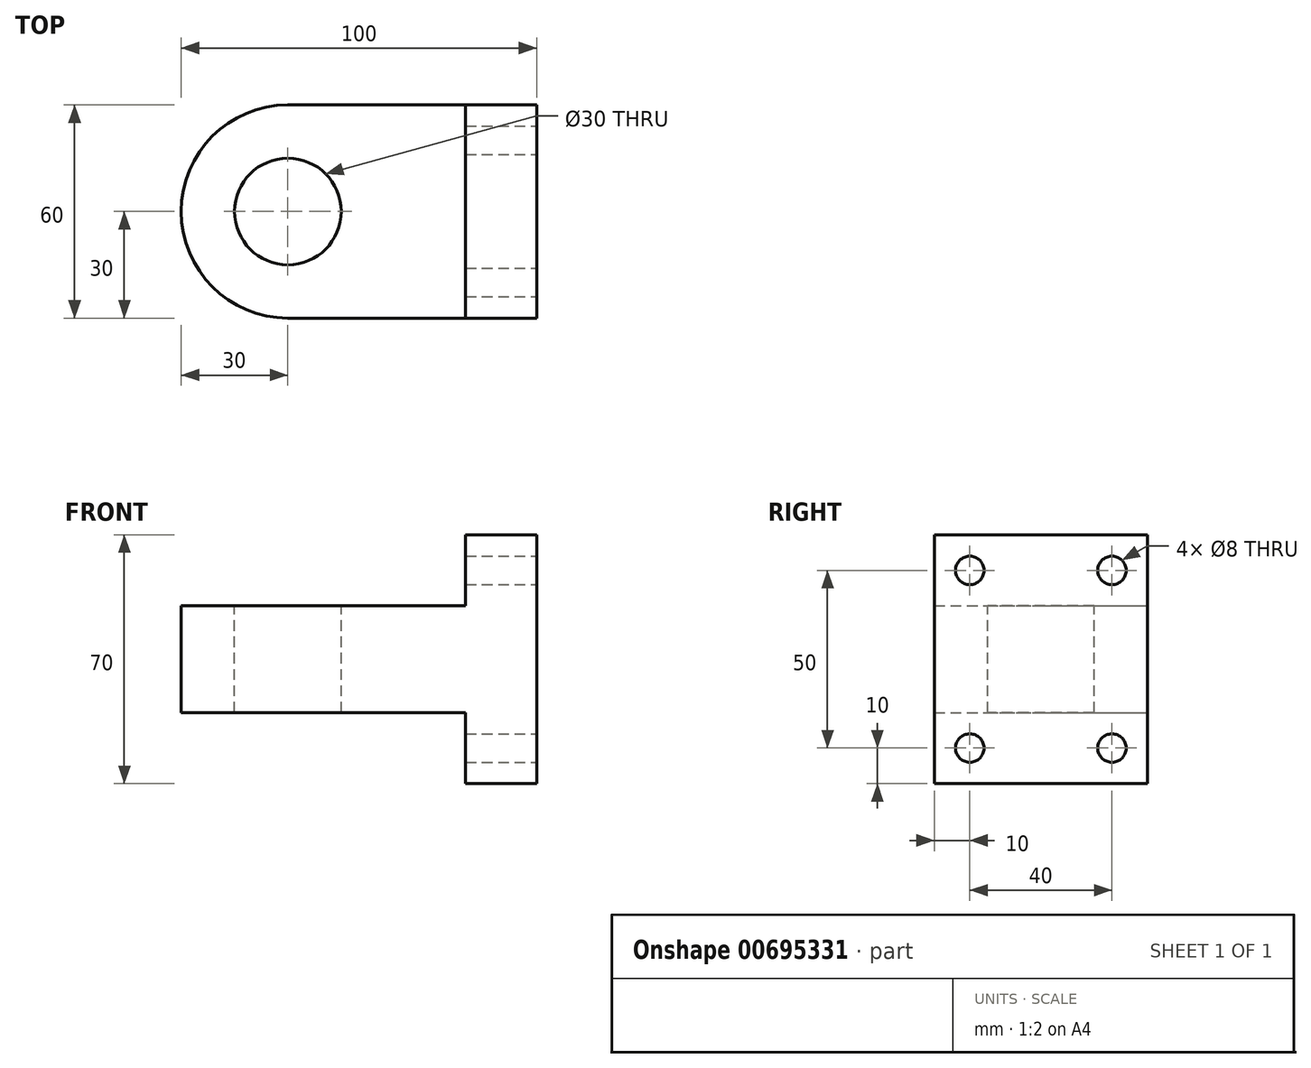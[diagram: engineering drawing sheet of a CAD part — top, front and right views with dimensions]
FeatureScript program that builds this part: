
annotation { "Feature Type Name" : "Feature", "Feature Type Description" : "" }
export const myFeature = defineFeature(function(context is Context, id is Id, definition is map)
    precondition{}
    {
        {
            var Q0;
            Q0=qCreatedBy(makeId("Front.planeOp"),FACE);
            var sketch = newSketch(context, id + "F0", { "sketchPlane" : qUnion([Q0])});
            skLineSegment(sketch, "E0", {"start": v(0, 0) * mm, "end": v(0, 35) * mm});
            skLineSegment(sketch, "E1", {"start": v(0, 35) * mm, "end": v(-20, 35) * mm});
            skLineSegment(sketch, "E2", {"start": v(-20, 35) * mm, "end": v(-20, 15) * mm});
            skLineSegment(sketch, "E3", {"start": v(-20, 15) * mm, "end": v(-100, 15) * mm});
            skLineSegment(sketch, "E4", {"start": v(-100, 15) * mm, "end": v(-100, 0) * mm});
            skLineSegment(sketch, "E5", {"start": v(-100, 0) * mm, "end": v(0, 0) * mm});
            skSolve(sketch);
        }
        {
            var Q0;
            Q0=makeQuery(id+"F0.imprint","IMPRINT",FACE,{"disambiguationData":[TD([[makeQuery(id+"F0.imprint","IMPRINT",EDGE,{"derivedFrom":sQuery(id+"F0.wireOp",EDGE,"E0")}),1.0]])]});
            extrude(context, id + "F1", {"entities" : qUnion([Q0]), "endBound" : BoundingType.SYMMETRIC, "depth" : 60 * mm, "offsetDistance" : 25 * mm});
        }
        {
            var Q0;
            Q0=makeQuery(id+"F1.opExtrude","CAP_EDGE",EDGE,{"disambiguationData":[OSD([sQuery(id+"F0.wireOp",EDGE,"E4")])],"isStart":false});
            fillet(context, id + "F2", {"entities" : qUnion([Q0]), "radius" : 30 * mm, "tangentPropagation" : true, "allowEdgeOverflow" : false});
        }
        {
            var Q0;
            Q0=makeQuery(id+"F1.opExtrude","CAP_EDGE",EDGE,{"disambiguationData":[OSD([sQuery(id+"F0.wireOp",EDGE,"E4")])],"isStart":true});
            fillet(context, id + "F3", {"entities" : qUnion([Q0]), "radius" : 30 * mm, "tangentPropagation" : true, "allowEdgeOverflow" : false});
        }
        {
            var Q0;
            Q0=makeQuery(id+"F1.opExtrude","SWEPT_FACE",FACE,{"disambiguationData":[OSD([sQuery(id+"F0.wireOp",EDGE,"E3")])]});
            var sketch = newSketch(context, id + "F4", { "sketchPlane" : qUnion([Q0])});
            skCircle(sketch, "E6", {"center": v(-70, 0) * mm, "radius": 15 * mm});
            skSolve(sketch);
        }
        {
            var Q0;
            Q0=makeQuery(id+"F4.imprint","IMPRINT",FACE,{"disambiguationData":[TD([[makeQuery(id+"F4.imprint","IMPRINT",EDGE,{"derivedFrom":sQuery(id+"F4.wireOp",EDGE,"E6")}),1.0]])]});
            extrude(context, id + "F5", {"entities" : qUnion([Q0]), "operationType" : NewBodyOperationType.REMOVE, "endBound" : BoundingType.UP_TO_NEXT, "oppositeDirection" : true, "depth" : 25 * mm, "offsetDistance" : 25 * mm});
        }
        {
            var Q0;
            Q0=makeQuery(id+"F1.opExtrude","SWEPT_BODY",BODY,{"disambiguationData":[OSD([sQuery(id+"F0.wireOp",EDGE,"E0"),sQuery(id+"F0.wireOp",EDGE,"E1"),sQuery(id+"F0.wireOp",EDGE,"E2"),sQuery(id+"F0.wireOp",EDGE,"E3"),sQuery(id+"F0.wireOp",EDGE,"E4"),sQuery(id+"F0.wireOp",EDGE,"E5")])]});
            var Q1;
            Q1=qCreatedBy(makeId("Top.planeOp"),FACE);
            mirror(context, id + "F6", {"operationType" : NewBodyOperationType.ADD, "entities" : qUnion([Q0]), "mirrorPlane" : qUnion([Q1])});
        }
        {
            var Q0;
            {var subQ0=makeQuery(id+"F1.opExtrude","SWEPT_FACE",FACE,{"disambiguationData":[OSD([sQuery(id+"F0.wireOp",EDGE,"E0")])]});Q0=makeQuery(id+"F6.boolean.opBoolean","MERGE",FACE,{"derivedFrom":[subQ0,makeQuery(id+"F6.opPattern","COPY",FACE,{"derivedFrom":subQ0,"instanceName":"1"})]});}
            var sketch = newSketch(context, id + "F7", { "sketchPlane" : qUnion([Q0])});
            skLineSegment(sketch, "E7", {"start": v(-30, -35) * mm, "end": v(-30, -25) * mm});
            skLineSegment(sketch, "E8", {"start": v(-30, -25) * mm, "end": v(-20, -25) * mm});
            skCircle(sketch, "E9", {"center": v(-20, -25) * mm, "radius": 4 * mm});
            skCircle(sketch, "E10.0.1.0", {"center": v(-20, 25) * mm, "radius": 4 * mm});
            skCircle(sketch, "E10.1.0.0", {"center": v(20, -25) * mm, "radius": 4 * mm});
            skCircle(sketch, "E10.1.1.0", {"center": v(20, 25) * mm, "radius": 4 * mm});
            skLineSegment(sketch, "E10.direction1", {"start": v(-20, -25) * mm, "end": v(20, -25) * mm, "construction": true});
            skLineSegment(sketch, "E10.direction2", {"start": v(-20, -25) * mm, "end": v(-20, 25) * mm, "construction": true});
            skSolve(sketch);
        }
        {
            var Q0;
            Q0 = qSketchRegion(id + "F7", true);
            extrude(context, id + "F8", {"entities" : qUnion([Q0]), "operationType" : NewBodyOperationType.REMOVE, "endBound" : BoundingType.UP_TO_NEXT, "oppositeDirection" : true, "depth" : 25 * mm, "offsetDistance" : 25 * mm});
        }
    });
